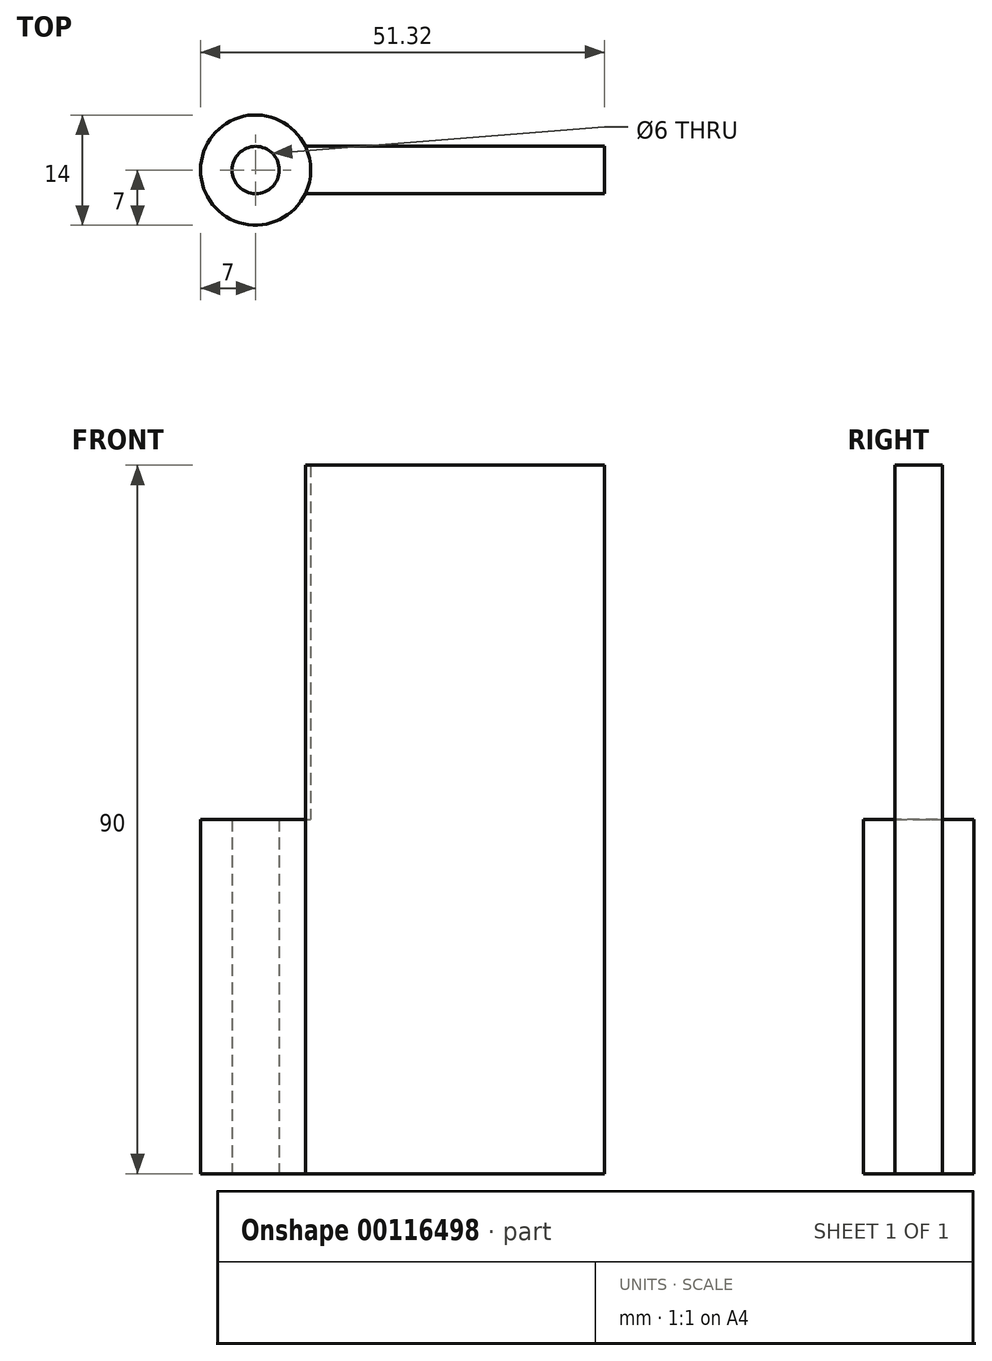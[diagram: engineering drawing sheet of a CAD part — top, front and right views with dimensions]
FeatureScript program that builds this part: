
annotation { "Feature Type Name" : "Feature", "Feature Type Description" : "" }
export const myFeature = defineFeature(function(context is Context, id is Id, definition is map)
    precondition{}
    {
        {
            var Q0;
            Q0=qCreatedBy(makeId("Top.planeOp"),FACE);
            var sketch = newSketch(context, id + "F0", { "sketchPlane" : qUnion([Q0])});
            skCircle(sketch, "E0", {"center": v(0, 0) * mm, "radius": 3 * mm});
            skCircle(sketch, "E1", {"center": v(0, 0) * mm, "radius": 7 * mm});
            skLineSegment(sketch, "E2", {"start": v(0, 0) * mm, "end": v(7, 0) * mm});
            skPoint(sketch, "E3", {"position": v(6.32, 3) * mm});
            skPoint(sketch, "E4.MirrorP", {"position": v(6.32, -3) * mm});
            skPoint(sketch, "E5", {"position": v(44.32, 3) * mm});
            skPoint(sketch, "E6.MirrorP", {"position": v(44.32, -3) * mm});
            skLineSegment(sketch, "E7", {"start": v(6.32, 3) * mm, "end": v(44.32, 3) * mm});
            skLineSegment(sketch, "E8", {"start": v(44.32, 3) * mm, "end": v(44.32, -3) * mm});
            skLineSegment(sketch, "E9", {"start": v(44.32, -3) * mm, "end": v(6.32, -3) * mm});
            skSolve(sketch);
        }
        {
            var Q0;
            {var subQ0=sQuery(id+"F0.wireOp",EDGE,"E7");Q0=makeQuery(id+"F0.imprint","IMPRINT",FACE,{"disambiguationData":[TD([[makeQuery(id+"F0.imprint","IMPRINT",EDGE,{"derivedFrom":subQ0}),-1.0]])]});}
            extrude(context, id + "F1", {"entities" : qUnion([Q0]), "depth" : 90 * mm});
        }
        {
            var Q0;
            Q0=makeQuery(id+"F0.imprint","IMPRINT",FACE,{"disambiguationData":[TD([[makeQuery(id+"F0.imprint","IMPRINT",EDGE,{"derivedFrom":sQuery(id+"F0.wireOp",EDGE,"E0")}),-1.0]])]});
            extrude(context, id + "F2", {"entities" : qUnion([Q0]), "operationType" : NewBodyOperationType.ADD, "depth" : 45 * mm});
        }
    });
